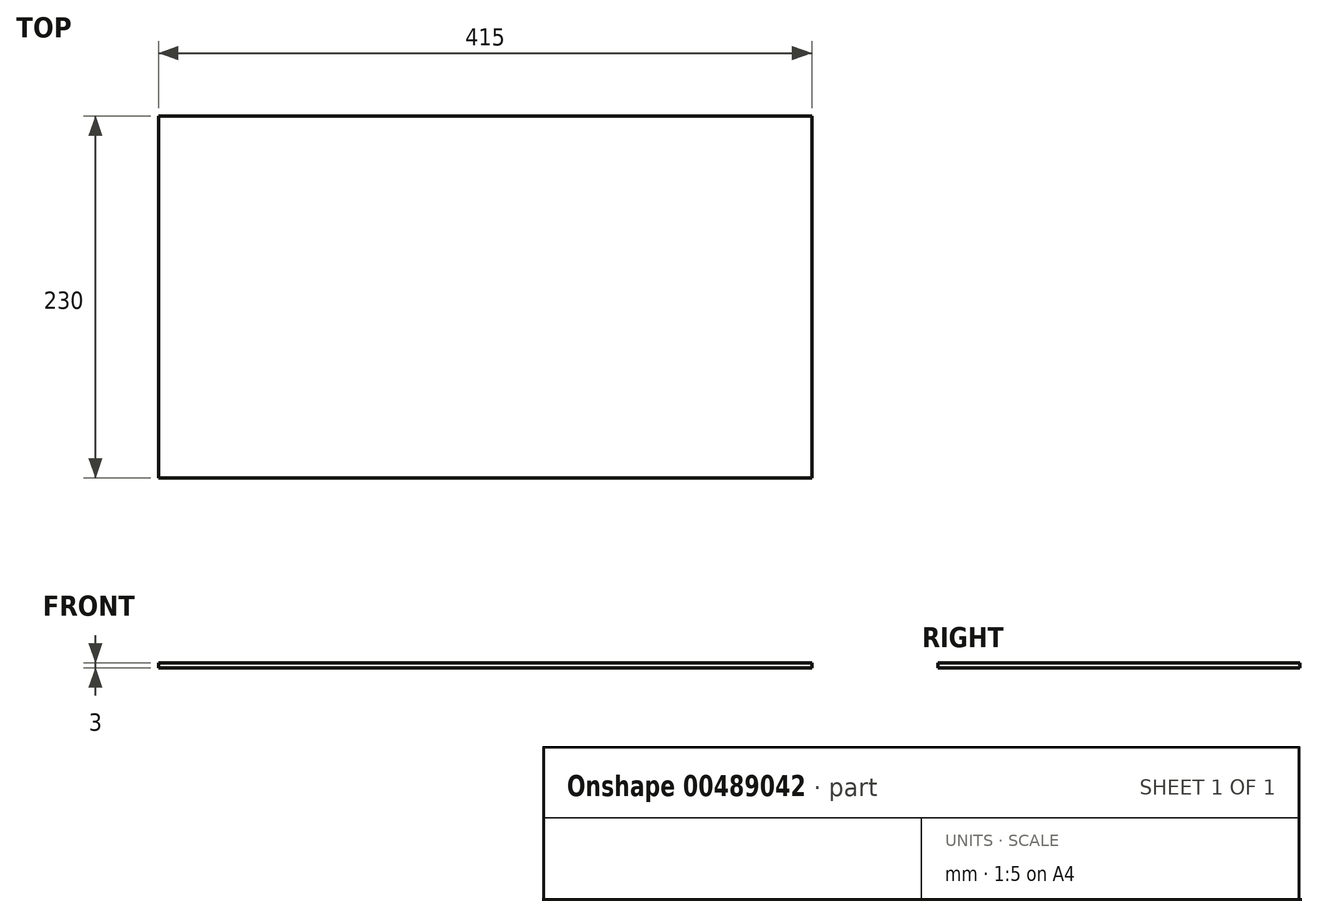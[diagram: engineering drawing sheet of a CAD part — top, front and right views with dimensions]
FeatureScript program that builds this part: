
annotation { "Feature Type Name" : "Feature", "Feature Type Description" : "" }
export const myFeature = defineFeature(function(context is Context, id is Id, definition is map)
    precondition{}
    {
        {
            var Q0;
            Q0=qCreatedBy(makeId("Top.planeOp"),FACE);
            var sketch = newSketch(context, id + "F0", { "sketchPlane" : qUnion([Q0])});
            skLineSegment(sketch, "E0.bottom", {"start": v(-197.16, 102.9) * mm, "end": v(217.84, 102.9) * mm});
            skLineSegment(sketch, "E0.top", {"start": v(-197.16, -127.1) * mm, "end": v(217.84, -127.1) * mm});
            skLineSegment(sketch, "E0.left", {"start": v(-197.16, 102.9) * mm, "end": v(-197.16, -127.1) * mm});
            skLineSegment(sketch, "E0.right", {"start": v(217.84, 102.9) * mm, "end": v(217.84, -127.1) * mm});
            skSolve(sketch);
        }
        {
            var Q0;
            Q0=makeQuery(id+"F0.imprint","IMPRINT",FACE,{"disambiguationData":[TD([[makeQuery(id+"F0.imprint","IMPRINT",EDGE,{"derivedFrom":sQuery(id+"F0.wireOp",EDGE,"E0.bottom")}),-1.0]])]});
            extrude(context, id + "F1", {"entities" : qUnion([Q0]), "depth" : 3 * mm});
        }
    });
